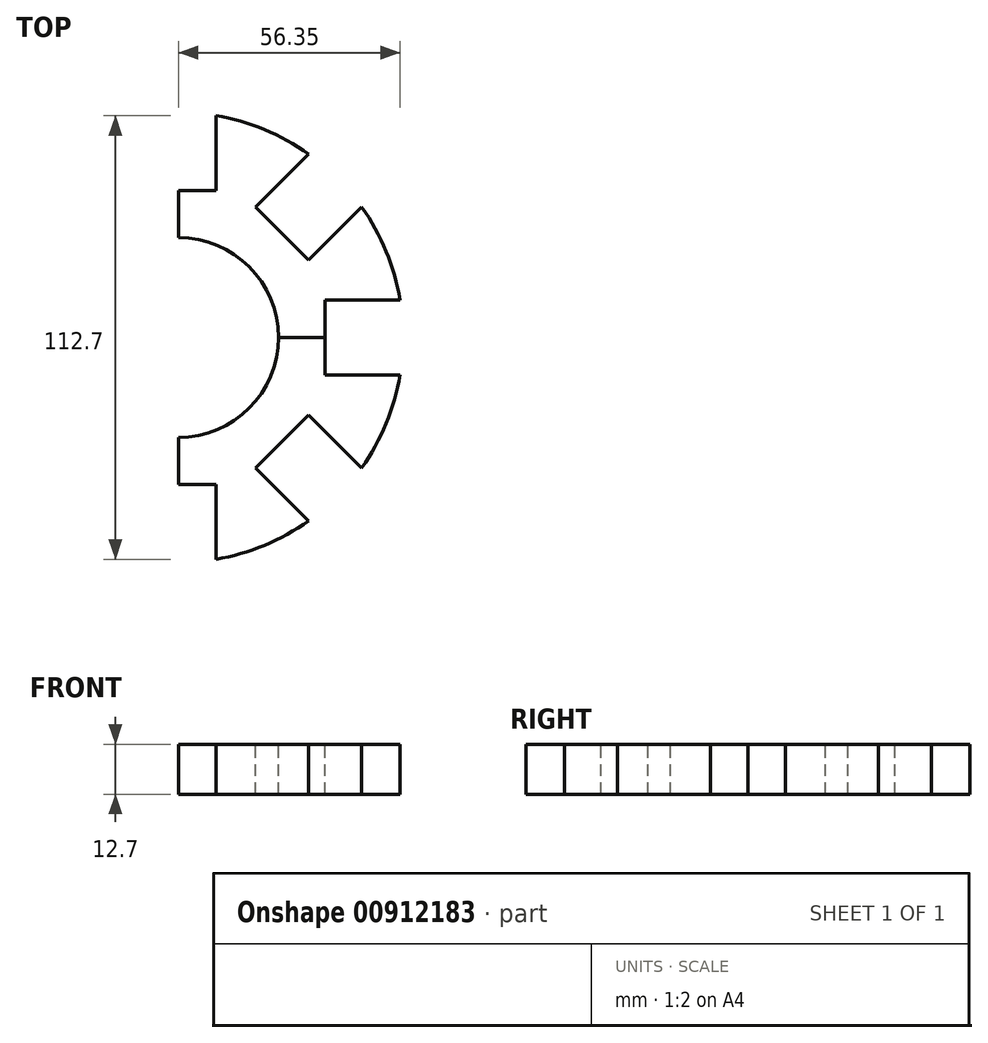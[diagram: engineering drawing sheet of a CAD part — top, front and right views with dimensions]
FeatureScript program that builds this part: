
annotation { "Feature Type Name" : "Feature", "Feature Type Description" : "" }
export const myFeature = defineFeature(function(context is Context, id is Id, definition is map)
    precondition{}
    {
        {
            var Q0;
            Q0=qCreatedBy(makeId("Top.planeOp"),FACE);
            var sketch = newSketch(context, id + "F0", { "sketchPlane" : qUnion([Q0])});
            skArc(sketch, "E0", {"start": v(21.87, 52.8) * mm, "mid": v(15.8, 54.92) * mm, "end": v(9.52, 56.35) * mm});
            skLineSegment(sketch, "E1", {"start": v(9.72, 23.47) * mm, "end": v(21.87, 52.8) * mm});
            skLineSegment(sketch, "E2.top", {"start": v(0, 37.3) * mm, "end": v(9.52, 37.3) * mm});
            skLineSegment(sketch, "E2.right", {"start": v(9.53, 66.26) * mm, "end": v(9.53, 37.3) * mm});
            skArc(sketch, "E3", {"start": v(9.72, 23.47) * mm, "mid": v(4.96, 24.91) * mm, "end": v(0, 25.4) * mm});
            skArc(sketch, "E4.MirrorCS", {"start": v(21.87, 52.8) * mm, "mid": v(27.67, 50) * mm, "end": v(33.11, 46.58) * mm});
            skLineSegment(sketch, "E5.MirrorCS", {"start": v(23.47, 9.72) * mm, "end": v(52.8, 21.87) * mm});
            skLineSegment(sketch, "E6.MirrorCS", {"start": v(40.12, 53.6) * mm, "end": v(19.64, 33.11) * mm});
            skArc(sketch, "E7.MirrorCS", {"start": v(9.72, 23.47) * mm, "mid": v(17.96, 17.96) * mm, "end": v(23.47, 9.72) * mm});
            skLineSegment(sketch, "E8.MirrorCS", {"start": v(53.6, 40.12) * mm, "end": v(33.11, 19.64) * mm});
            skLineSegment(sketch, "E9.MirrorCS", {"start": v(33.11, 19.64) * mm, "end": v(19.64, 33.11) * mm});
            skLineSegment(sketch, "E10.MirrorCS", {"start": v(37.3, 9.53) * mm, "end": v(37.3, 0) * mm});
            skArc(sketch, "E11.MirrorCS", {"start": v(25.4, 0) * mm, "mid": v(24.91, 4.96) * mm, "end": v(23.47, 9.72) * mm});
            skLineSegment(sketch, "E12.MirrorCS", {"start": v(56.35, 9.53) * mm, "end": v(37.3, 9.53) * mm});
            skPoint(sketch, "E13.end.orphan", {"position": v(9.53, 56.35) * mm});
            skPoint(sketch, "E13.start.orphan", {"position": v(-9.53, 56.35) * mm});
            skLineSegment(sketch, "E14", {"start": v(0, 25.4) * mm, "end": v(0, 37.3) * mm});
            skLineSegment(sketch, "E15", {"start": v(25.4, 0) * mm, "end": v(37.3, 0) * mm});
            skPoint(sketch, "E16.orphan", {"position": v(-9.53, 37.3) * mm});
            skPoint(sketch, "E17.orphan", {"position": v(33.11, 46.58) * mm});
            skArc(sketch, "E18.trimOffspring", {"start": v(46.58, 33.11) * mm, "mid": v(50, 27.67) * mm, "end": v(52.8, 21.87) * mm});
            skPoint(sketch, "E19.MirrorCS.start.orphan", {"position": v(46.58, 33.11) * mm});
            skArc(sketch, "E20.trimOffspring", {"start": v(56.35, 9.52) * mm, "mid": v(54.92, 15.8) * mm, "end": v(52.8, 21.87) * mm});
            skLineSegment(sketch, "E21.trimOffspring", {"start": v(56.35, 0) * mm, "end": v(57.15, 0) * mm});
            skSolve(sketch);
        }
        {
            var Q0;
            {var subQ1=sQuery(id+"F0.wireOp",EDGE,"E1");Q0=makeQuery(id+"F0.imprint","IMPRINT",FACE,{"disambiguationData":[TD([[makeQuery(id+"F0.imprint","IMPRINT",EDGE,{"derivedFrom":subQ1}),1.0]])]});}
            extrude(context, id + "F1", {"entities" : qUnion([Q0]), "oppositeDirection" : true, "depth" : 12.7 * mm, "offsetDistance" : 25.4 * mm});
        }
        {
            var Q0;
            Q0=qCreatedBy(makeId("Front.planeOp"),FACE);
            var sketch = newSketch(context, id + "F2", { "sketchPlane" : qUnion([Q0])});
            skLineSegment(sketch, "E22", {"start": v(0, 0) * mm, "end": v(0, -47.26) * mm});
            skSolve(sketch);
        }
        {
            var Q0;
            Q0 = qSketchRegion(id + "F0", true);
            extrude(context, id + "F3", {"entities" : qUnion([Q0]), "operationType" : NewBodyOperationType.ADD, "oppositeDirection" : true, "depth" : 12.7 * mm, "offsetDistance" : 25.4 * mm});
        }
        {
            var Q0;
            Q0=makeQuery(id+"F1.opExtrude","SWEPT_BODY",BODY,{"disambiguationData":[OSD([sQuery(id+"F0.wireOp",EDGE,"E0"),sQuery(id+"F0.wireOp",EDGE,"E1"),sQuery(id+"F0.wireOp",EDGE,"E2.top"),sQuery(id+"F0.wireOp",EDGE,"E2.right"),sQuery(id+"F0.wireOp",EDGE,"E3"),sQuery(id+"F0.wireOp",EDGE,"E14")])]});
            var Q1;
            Q1=sQuery(id+"F2.wireOp",EDGE,"E22");
            circularPattern(context, id + "F4", {"entities" : qUnion([Q0]), "axis" : qUnion([Q1]), "angle" : 90 * degree, "instanceCount" : 2, "equalSpace" : true});
        }
    });
